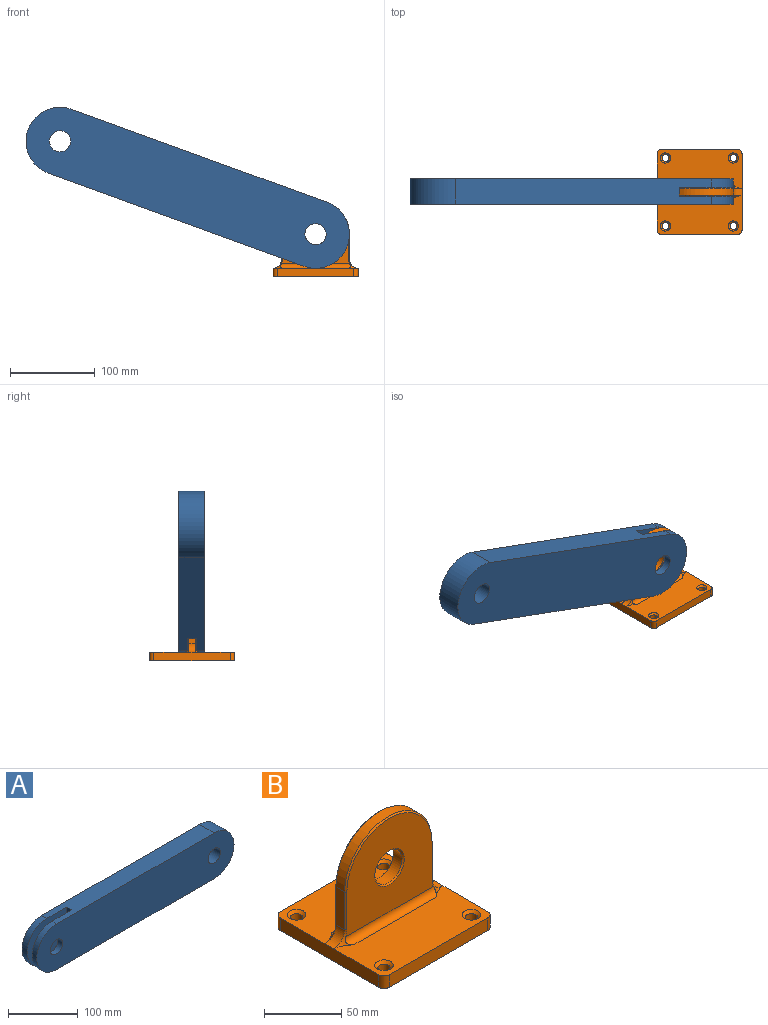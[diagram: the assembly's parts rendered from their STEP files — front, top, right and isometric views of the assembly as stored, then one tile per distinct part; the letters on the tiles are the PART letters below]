
ASSEMBLY  parts=2 mates=1
PART A: 13 faces, bbox 400x30x80 mm
  f0: cylinder r=40mm len=80mm, axis (0,1,0), area 1311.1mm2, adj f2,f3,f4,f5
  f1: cylinder r=12.5mm len=25mm, axis (0,1,0), area 819.4mm2, adj f4,f5
  f2: plane 320x30mm, normal (0,0,1), area 9200mm2, adj f0,f4,f5,f6,f7,f9,f10,f12
  f3: plane 320x30mm, normal (0,0,-1), area 9200mm2, adj f0,f4,f5,f6,f7,f9,f10,f12
  f4: plane 400x80mm, normal (0,1,0), area 29644.8mm2, adj f0,f1,f2,f3,f11,f12
  f5: plane 80x80mm, normal (0,-1,0), area 5222.4mm2, adj f0,f1,f2,f3,f10
  f6: cylinder r=40mm len=80mm, axis (0,1,0), area 1202.2mm2, adj f2,f3,f7,f9
  f7: plane 400x80mm, normal (0,-1,0), area 29644.8mm2, adj f2,f3,f6,f8,f11,f12
  f8: cylinder r=12.5mm len=25mm, axis (0,1,0), area 751.4mm2, adj f7,f9
  f9: plane 80x80mm, normal (0,1,0), area 5222.4mm2, adj f2,f3,f6,f8,f10
  f10: plane 80x10mm, normal (-1,0,0), area 800mm2, adj f2,f3,f5,f9
  f11: cylinder r=12.5mm len=30mm, axis (0,1,0), area 2356.2mm2, adj f4,f7
  f12: cylinder r=40mm len=80mm, axis (0,1,0), area 3769.9mm2, adj f2,f3,f4,f7
PART B: 41 faces, bbox 100x100x90 mm
  f0: plane 80.4x74mm, normal (0,-1,0), area 4550.5mm2, adj f27,f34,f35,f36,f37,f38,f39
  f1: plane 80.4x74mm, normal (0,1,0), area 4550.5mm2, adj f28,f29,f30,f31,f32,f33,f40
  f2: plane 30x8mm, normal (1,0,0), area 240mm2, adj f12,f13,f32,f37
  f3: plane 30x8mm, normal (-1,0,0), area 240mm2, adj f11,f13,f30,f35
  f4: plane 100x46mm, normal (0,0,1), area 3858.2mm2, adj f6,f8,f9,f15,f18,f25,f26,f34
  f5: plane 100x46mm, normal (0,0,1), area 3858.2mm2, adj f6,f7,f8,f16,f17,f23,f24,f29
  f6: plane 90x10mm, normal (1,0,0), area 900mm2, adj f4,f5,f10,f12,f16,f18
  f7: plane 90x10mm, normal (0,1,0), area 900mm2, adj f5,f10,f16,f17
  f8: plane 90x10mm, normal (-1,0,0), area 900mm2, adj f4,f5,f10,f11,f15,f17
  f9: plane 90x10mm, normal (0,-1,0), area 900mm2, adj f4,f10,f15,f18
  f10: plane 100x100mm, normal (0,0,-1), area 9777.5mm2, adj f6,f7,f8,f9,f15,f16,f17,f18
  f11: cylinder r=10mm len=10mm, axis (0,-1,0), area 125.7mm2, adj f3,f8,f29,f34
  f12: cylinder r=10mm len=10mm, axis (0,1,0), area 125.7mm2, adj f2,f6,f33,f38
  f13: cylinder r=40mm len=80mm, axis (0,-1,0), area 1005.3mm2, adj f2,f3,f31,f36
  f14: cylinder r=12.5mm len=25mm, axis (0,-1,0), area 628.3mm2, adj f27,f28
  f15: cylinder r=5mm len=10mm, axis (0,0,1), area 78.5mm2, adj f4,f8,f9,f10
  f16: cylinder r=5mm len=10mm, axis (0,0,1), area 78.5mm2, adj f5,f6,f7,f10
  f17: cylinder r=5mm len=10mm, axis (0,0,-1), area 78.5mm2, adj f5,f7,f8,f10
  f18: cylinder r=5mm len=10mm, axis (0,0,-1), area 78.5mm2, adj f4,f6,f9,f10
  f19: cylinder r=4mm len=8mm, axis (0,0,1), area 201.1mm2, adj f10,f24
  f20: cylinder r=4mm len=8mm, axis (0,0,1), area 201.1mm2, adj f10,f23
  f21: cylinder r=4mm len=8mm, axis (0,0,1), area 201.1mm2, adj f10,f25
  f22: cylinder r=4mm len=8mm, axis (0,0,1), area 201.1mm2, adj f10,f26
  f23: cone r=4mm half-angle=45deg, axis (0,0,1), area 88.9mm2, adj f5,f20
  f24: cone r=4mm half-angle=45deg, axis (0,0,1), area 88.9mm2, adj f5,f19
  f25: cone r=4mm half-angle=45deg, axis (0,0,1), area 88.9mm2, adj f4,f21
  f26: cone r=4mm half-angle=45deg, axis (0,0,1), area 88.9mm2, adj f4,f22
  f27: cone r=12.5mm half-angle=45deg, axis (0,-1,0), area 115.5mm2, adj f0,f14
  f28: cone r=13.5mm half-angle=45deg, axis (0,1,0), area 115.5mm2, adj f1,f14
  f29: cone r=11mm half-angle=45deg, axis (0,1,0), area 30.4mm2, adj f1,f5,f11,f30,f40
  f30: plane 30x1mm, normal (-0.71,0.71,0), area 42.4mm2, adj f1,f3,f29,f31
  f31: cone r=40mm half-angle=45deg, axis (0,-1,0), area 175.5mm2, adj f1,f13,f30,f32
  f32: plane 30x1mm, normal (0.71,0.71,0), area 42.4mm2, adj f1,f2,f31,f33
  f33: cone r=11mm half-angle=45deg, axis (0,1,0), area 30.4mm2, adj f1,f5,f12,f32,f40
  f34: cone r=11mm half-angle=45deg, axis (0,-1,0), area 30.4mm2, adj f0,f4,f11,f35,f39
  f35: plane 30x1mm, normal (-0.71,-0.71,0), area 42.4mm2, adj f0,f3,f34,f36
  f36: cone r=39mm half-angle=45deg, axis (0,1,0), area 175.5mm2, adj f0,f13,f35,f37
  f37: plane 30x1mm, normal (0.71,-0.71,0), area 42.4mm2, adj f0,f2,f36,f38
  f38: cone r=11mm half-angle=45deg, axis (0,-1,0), area 30.4mm2, adj f0,f4,f12,f37,f39
  f39: cylinder r=5mm len=82.14mm, axis (1,0,0), area 631.2mm2, adj f0,f4,f34,f38
  f40: cylinder r=5mm len=82.14mm, axis (-1,0,0), area 631.2mm2, adj f1,f5,f29,f33
PLACE A rot(axis=(0,-1,0),160deg) t=(-260.35,-59.29,-45.04)mm
PLACE B t=(-110,-74.72,-149.76)mm fixed
MATE revolute A.f1 <-> B.f14  axis (0,1,0) through (-110,-79.72,-99.76)mm
